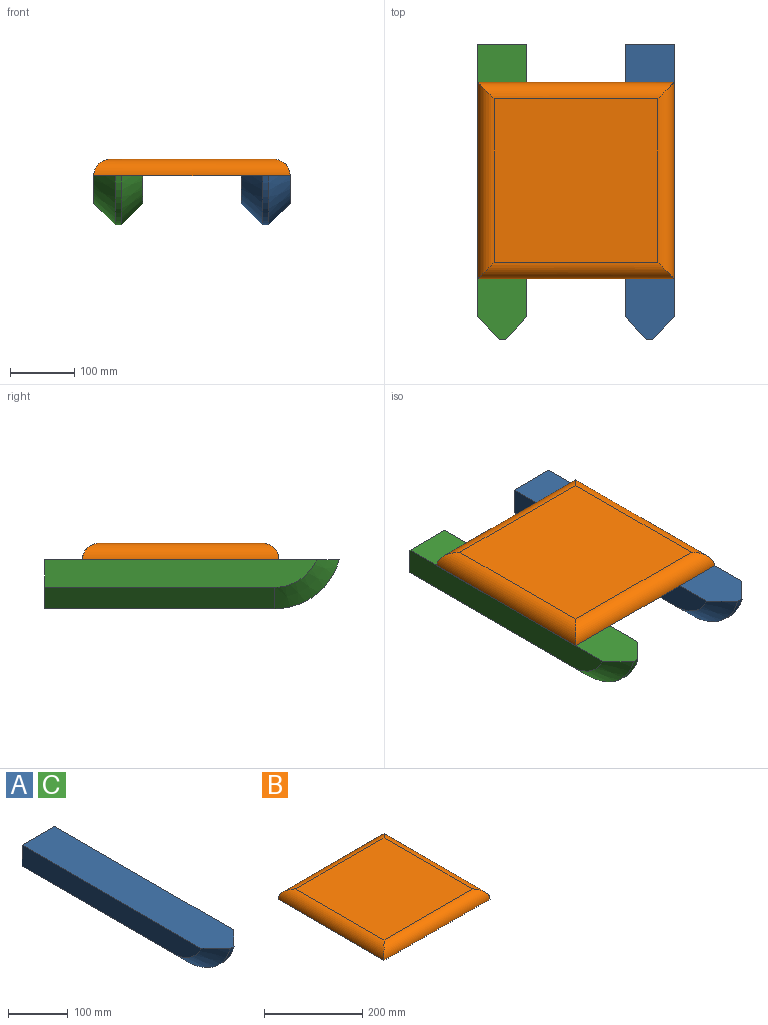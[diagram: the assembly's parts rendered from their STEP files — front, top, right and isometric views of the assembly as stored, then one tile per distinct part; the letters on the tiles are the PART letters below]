
ASSEMBLY  parts=3 mates=2
PART A: 10 faces, bbox 76.2x457.2x85 mm
  f0: plane 457.2x76.2mm, normal (0,0,1), area 33673.3mm2, adj f1,f3,f4,f5,f7,f9
  f1: plane 421.98x42.86mm, normal (-1,0,0), area 17315mm2, adj f0,f4,f6,f7
  f2: plane 357.22x9.53mm, normal (0,0,-1), area 3402.5mm2, adj f4,f5,f6,f8
  f3: plane 421.98x42.86mm, normal (1,0,0), area 17315mm2, adj f0,f4,f8,f9
  f4: plane 76.2x76.2mm, normal (0,1,0), area 4695.1mm2, adj f0,f1,f2,f3,f6,f8
  f5: cylinder r=103.7mm len=99.98mm, axis (-1,0,0), area 1286.4mm2, adj f0,f2,f7,f9
  f6: plane 357.22x33.34mm, normal (-0.71,0,-0.71), area 16841.5mm2, adj f1,f2,f4,f7
  f7: cone r=70.36mm half-angle=45deg, axis (1,0,0), area 5125.1mm2, adj f0,f1,f5,f6
  f8: plane 357.22x33.34mm, normal (0.71,0,-0.71), area 16841.5mm2, adj f2,f3,f4,f9
  f9: cone r=70.36mm half-angle=45deg, axis (-1,0,0), area 5125.1mm2, adj f0,f3,f5,f8
PART B: 6 faces, bbox 304.8x304.8x25.4 mm
  f0: plane 254x254mm, normal (0,0,1), area 64516mm2, adj f2,f3,f4,f5
  f1: plane 304.8x304.8mm, normal (0,0,-1), area 92903mm2, adj f2,f3,f4,f5
  f2: cylinder r=25.4mm len=304.8mm, axis (1,0,0), area 11424.5mm2, adj f0,f1,f3,f4
  f3: cylinder r=25.4mm len=304.8mm, axis (0,1,0), area 11424.5mm2, adj f0,f1,f2,f5
  f4: cylinder r=25.4mm len=304.8mm, axis (0,-1,0), area 11424.5mm2, adj f0,f1,f2,f5
  f5: cylinder r=25.4mm len=304.8mm, axis (-1,0,0), area 11424.5mm2, adj f0,f1,f3,f4
PART C: same geometry as A
PLACE A at identity
PLACE B t=(-228.6,152.4,0)mm
PLACE C t=(-228.6,0,0)mm
MATE fastened C.f0 <-> B.f1  axis (0,0,1) through (-319.75,-210.99,130.39)mm
MATE fastened B.f1 <-> A.f0  axis (0,0,-1) through (-14.95,-210.99,130.39)mm
